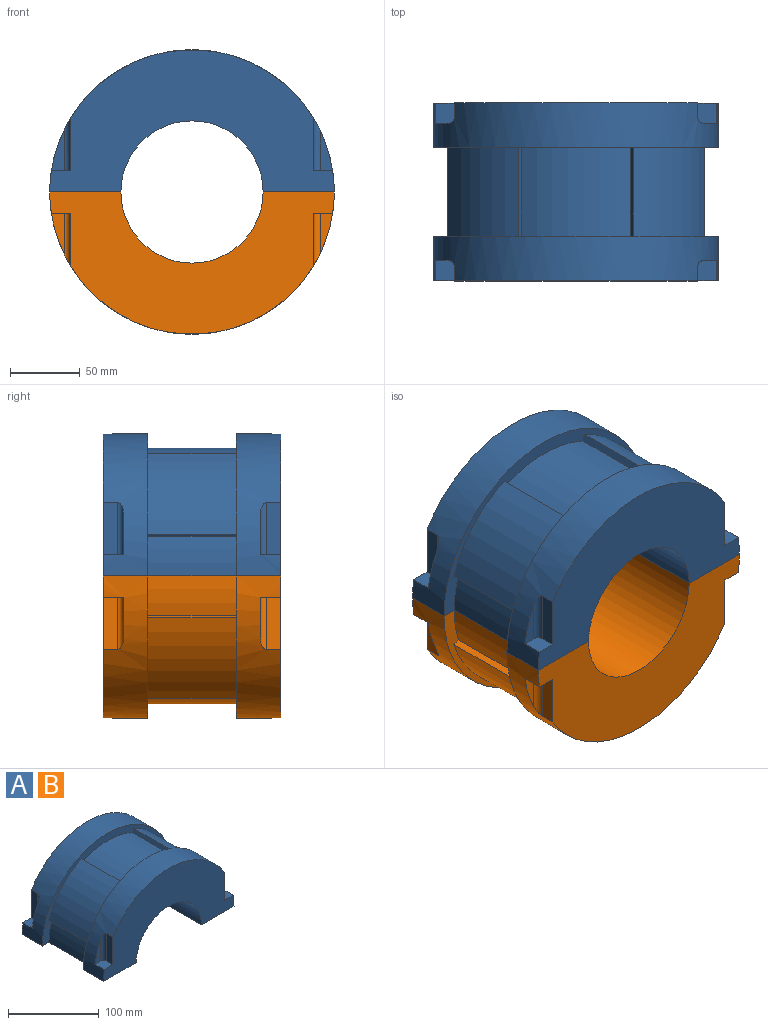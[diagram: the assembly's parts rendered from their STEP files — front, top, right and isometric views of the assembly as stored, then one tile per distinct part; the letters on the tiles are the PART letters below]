
ASSEMBLY  parts=2 mates=1
PART A: 34 faces, bbox 203.2x127x101.6 mm
  f0: plane 203.2x101.6mm, normal (0,-1,0), area 2297.5mm2, adj f1,f2,f4,f5,f7,f11,f28,f29
  f1: cylinder r=91.44mm len=77.29mm, axis (0,-1,0), area 5067.1mm2, adj f0,f10,f28,f31
  f2: cylinder r=91.44mm len=63.5mm, axis (0,-1,0), area 1824.1mm2, adj f0,f7,f10,f29
  f3: cylinder r=101.6mm len=203.2mm, axis (0,1,0), area 8987.9mm2, adj f5,f7,f8,f10,f12,f13,f14,f15
  f4: cylinder r=101.6mm len=203.2mm, axis (0,1,0), area 8987.1mm2, adj f0,f5,f7,f9,f16,f17,f18,f19
  f5: plane 127x50.8mm, normal (0,0,-1), area 5806.4mm2, adj f0,f3,f4,f6,f8,f9,f10,f11
  f6: cylinder r=50.8mm len=127mm, axis (0,1,0), area 20268.3mm2, adj f5,f7,f8,f9
  f7: plane 127x50.8mm, normal (0,0,-1), area 5806.4mm2, adj f0,f2,f3,f4,f6,f8,f9,f10
  f8: plane 203.2x101.6mm, normal (0,-1,0), area 11556.7mm2, adj f3,f5,f6,f7,f14,f15,f22,f23
  f9: plane 203.2x101.6mm, normal (0,1,0), area 11556.8mm2, adj f4,f5,f6,f7,f18,f19,f26,f27
  f10: plane 203.2x101.6mm, normal (0,1,0), area 2297.5mm2, adj f1,f2,f3,f5,f7,f11,f28,f29
  f11: cylinder r=91.44mm len=63.5mm, axis (0,-1,0), area 1824.1mm2, adj f0,f5,f10,f33
  f12: cylinder r=4.45mm len=37.25mm, axis (0,0,-1), area 256.6mm2, adj f3,f13,f14,f15
  f13: plane 27.84x8.44mm, normal (0,-1,0), area 137.8mm2, adj f3,f12,f15
  f14: plane 37.25x10.16mm, normal (1,0,0), area 378.4mm2, adj f3,f8,f12,f15
  f15: plane 14.61x13.46mm, normal (0,0,1), area 192mm2, adj f3,f8,f12,f13,f14
  f16: cylinder r=4.45mm len=37.24mm, axis (0,0,-1), area 245mm2, adj f4,f17,f18,f19
  f17: plane 28.69x8.84mm, normal (0,1,0), area 149.2mm2, adj f4,f16,f19
  f18: plane 37.24x10.16mm, normal (1,0,0), area 378.4mm2, adj f4,f9,f16,f19
  f19: plane 14.61x13.46mm, normal (0,0,1), area 192.2mm2, adj f4,f9,f16,f17,f18
  f20: plane 29.05x9.01mm, normal (0,-1,0), area 154.1mm2, adj f3,f21,f23
  f21: cylinder r=4.45mm len=37.24mm, axis (0,0,-1), area 240.1mm2, adj f3,f20,f22,f23
  f22: plane 37.24x10.16mm, normal (-1,0,0), area 378.4mm2, adj f3,f8,f21,f23
  f23: plane 14.61x13.46mm, normal (0,0,1), area 192.3mm2, adj f3,f8,f20,f21,f22
  f24: cylinder r=4.45mm len=37.24mm, axis (0,0,-1), area 240.1mm2, adj f4,f25,f26,f27
  f25: plane 29.05x9.01mm, normal (0,1,0), area 154.1mm2, adj f4,f24,f27
  f26: plane 37.24x10.16mm, normal (-1,0,0), area 378.4mm2, adj f4,f9,f24,f27
  f27: plane 14.61x13.46mm, normal (0,0,1), area 192.3mm2, adj f4,f9,f24,f25,f26
  f28: plane 63.5x4.6mm, normal (-0.91,0,0.42), area 322.6mm2, adj f0,f1,f10,f30
  f29: plane 63.5x4.83mm, normal (0.31,0,-0.95), area 322.6mm2, adj f0,f2,f10,f30
  f30: cylinder r=96.52mm len=63.5mm, axis (0,1,0), area 5027.7mm2, adj f0,f10,f28,f29
  f31: plane 63.5x4.6mm, normal (0.91,0,0.42), area 322.6mm2, adj f0,f1,f10,f32
  f32: cylinder r=96.52mm len=63.5mm, axis (0,1,0), area 5027.7mm2, adj f0,f10,f31,f33
  f33: plane 63.5x4.83mm, normal (-0.31,0,-0.95), area 322.6mm2, adj f0,f10,f11,f32
PART B: same geometry as A
PLACE A t=(-76.84,-3.62,10.32)mm
PLACE B rot(axis=(1,0,0),180deg) t=(-76.84,-3.62,10.32)mm
MATE planar B.f7 <-> A.f7  axis (0,0,1) through (-2.9,-3.62,10.32)mm
